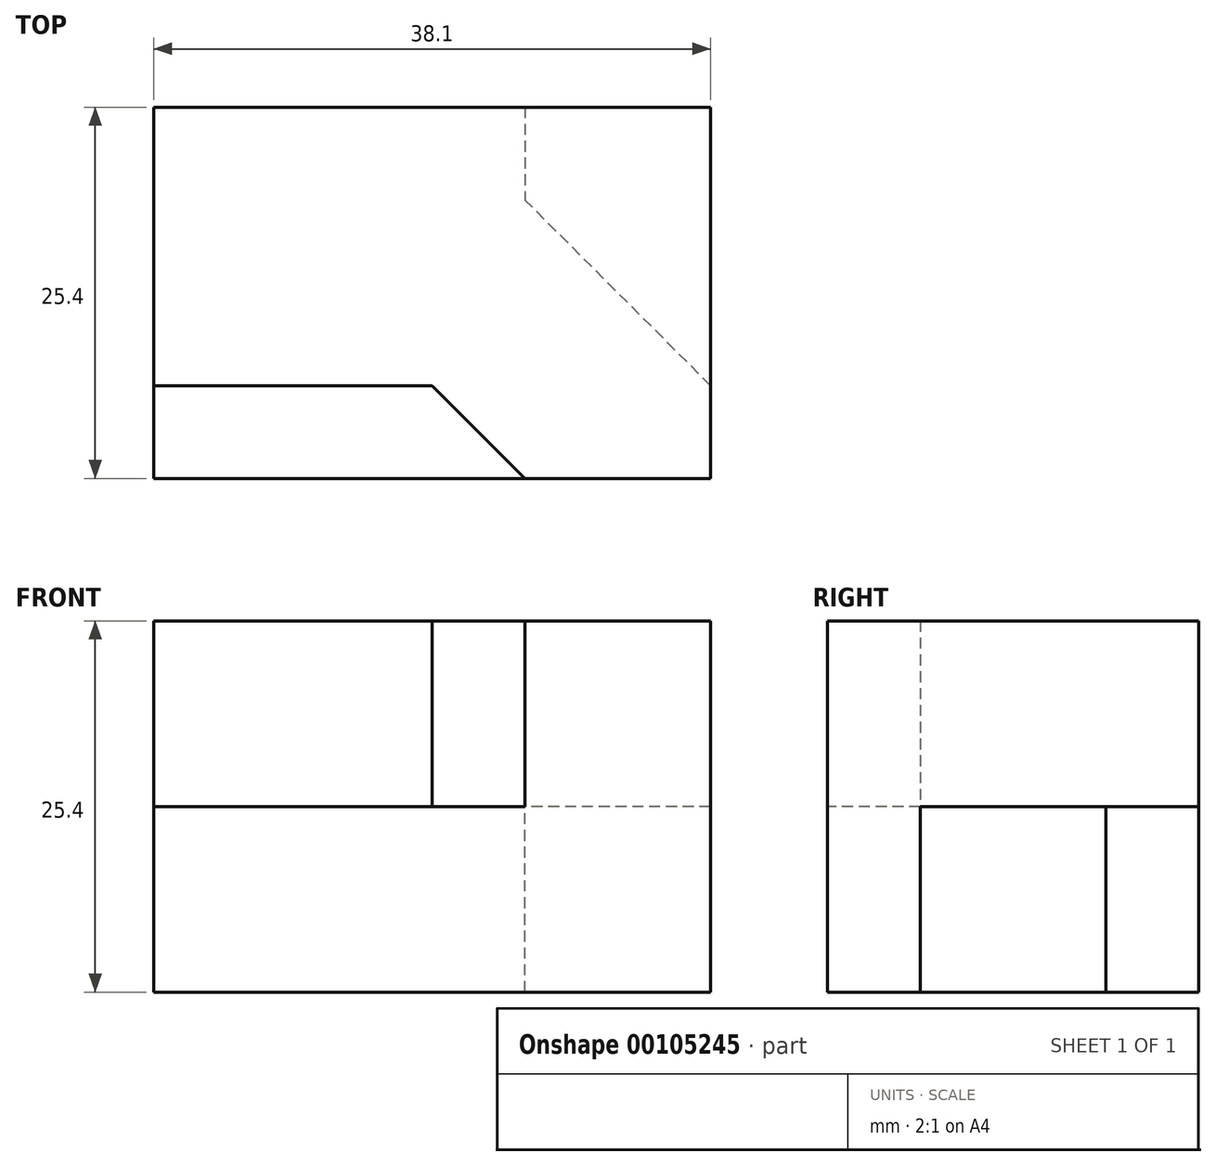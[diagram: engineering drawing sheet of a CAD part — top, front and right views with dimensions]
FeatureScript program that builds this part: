
annotation { "Feature Type Name" : "Feature", "Feature Type Description" : "" }
export const myFeature = defineFeature(function(context is Context, id is Id, definition is map)
    precondition{}
    {
        {
            var Q0;
            Q0=qCreatedBy(makeId("Front.planeOp"),FACE);
            var sketch = newSketch(context, id + "F0", { "sketchPlane" : qUnion([Q0])});
            skLineSegment(sketch, "E0", {"start": v(0, 0) * mm, "end": v(38.1, 0) * mm});
            skLineSegment(sketch, "E1", {"start": v(38.1, 0) * mm, "end": v(38.1, 12.7) * mm});
            skLineSegment(sketch, "E2", {"start": v(38.1, 12.7) * mm, "end": v(25.4, 12.7) * mm});
            skLineSegment(sketch, "E3", {"start": v(25.4, 12.7) * mm, "end": v(25.4, 25.4) * mm});
            skLineSegment(sketch, "E4", {"start": v(25.4, 25.4) * mm, "end": v(0, 25.4) * mm});
            skLineSegment(sketch, "E5", {"start": v(0, 25.4) * mm, "end": v(0, 0) * mm});
            skLineSegment(sketch, "E6", {"start": v(38.1, 12.7) * mm, "end": v(38.1, 25.4) * mm});
            skLineSegment(sketch, "E7", {"start": v(38.1, 25.4) * mm, "end": v(25.4, 25.4) * mm});
            skSolve(sketch);
        }
        {
            var Q0;
            Q0=qCreatedBy(makeId("Top.planeOp"),FACE);
            var sketch = newSketch(context, id + "F1", { "sketchPlane" : qUnion([Q0])});
            skLineSegment(sketch, "E8", {"start": v(0, 0) * mm, "end": v(0, 25.4) * mm});
            skLineSegment(sketch, "E9", {"start": v(0, 25.4) * mm, "end": v(38.1, 25.4) * mm});
            skLineSegment(sketch, "E10", {"start": v(38.1, 25.4) * mm, "end": v(38.1, 0) * mm});
            skLineSegment(sketch, "E11", {"start": v(38.1, 0) * mm, "end": v(0, 0) * mm});
            skLineSegment(sketch, "E12", {"start": v(0, 25.4) * mm, "end": v(25.4, 0) * mm});
            skLineSegment(sketch, "E13", {"start": v(38.1, 6.35) * mm, "end": v(19.05, 25.4) * mm});
            skLineSegment(sketch, "E14", {"start": v(38.1, 0) * mm, "end": v(38.1, 6.35) * mm});
            skSolve(sketch);
        }
        {
            var Q0;
            Q0=qCreatedBy(makeId("Right.planeOp"),FACE);
            var sketch = newSketch(context, id + "F2", { "sketchPlane" : qUnion([Q0])});
            skLineSegment(sketch, "E15", {"start": v(0, 0) * mm, "end": v(0, 12.7) * mm});
            skLineSegment(sketch, "E16", {"start": v(0, 12.7) * mm, "end": v(6.35, 12.7) * mm});
            skLineSegment(sketch, "E17", {"start": v(6.35, 12.7) * mm, "end": v(6.35, 25.4) * mm});
            skLineSegment(sketch, "E18", {"start": v(6.35, 25.4) * mm, "end": v(25.4, 25.4) * mm});
            skLineSegment(sketch, "E19", {"start": v(25.4, 25.4) * mm, "end": v(25.4, 0) * mm});
            skLineSegment(sketch, "E20", {"start": v(25.4, 0) * mm, "end": v(0, 0) * mm});
            skSolve(sketch);
        }
        {
            var Q0;
            {var subQ1=sQuery(id+"F1.wireOp",EDGE,"E12");Q0=makeQuery(id+"F1.imprint","IMPRINT",FACE,{"disambiguationData":[TD([[makeQuery(id+"F1.imprint","IMPRINT",EDGE,{"derivedFrom":subQ1}),1.0]])]});}
            extrude(context, id + "F3", {"entities" : qUnion([Q0]), "depth" : 25.4 * mm});
        }
        {
            var Q0;
            Q0=makeQuery(id+"F0.imprint","IMPRINT",FACE,{"disambiguationData":[TD([[makeQuery(id+"F0.imprint","IMPRINT",EDGE,{"derivedFrom":sQuery(id+"F0.wireOp",EDGE,"E2")}),-1.0]])]});
            extrude(context, id + "F4", {"entities" : qUnion([Q0]), "operationType" : NewBodyOperationType.ADD, "oppositeDirection" : true, "depth" : 25.4 * mm});
        }
        {
            var Q0;
            Q0 = qSketchRegion(id + "F2", true);
            extrude(context, id + "F5", {"entities" : qUnion([Q0]), "operationType" : NewBodyOperationType.ADD, "depth" : 25.4 * mm});
        }
    });
